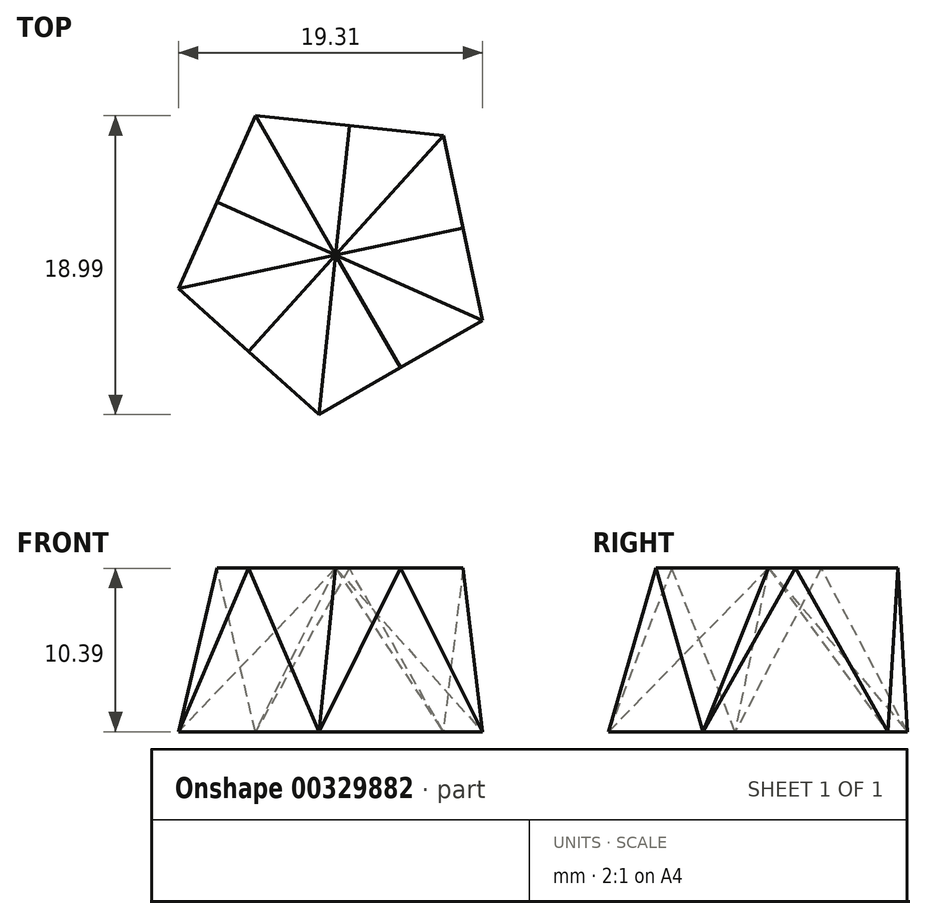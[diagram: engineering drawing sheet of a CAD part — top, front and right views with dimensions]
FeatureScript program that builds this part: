
annotation { "Feature Type Name" : "Feature", "Feature Type Description" : "" }
export const myFeature = defineFeature(function(context is Context, id is Id, definition is map)
    precondition{}
    {
        {
            var Q0;
            Q0=qCreatedBy(makeId("Top.planeOp"),FACE);
            var sketch = newSketch(context, id + "F0", { "sketchPlane" : qUnion([Q0])});
            skLineSegment(sketch, "E0", {"start": v(-6, -8.26) * mm, "end": v(6, -8.26) * mm});
            skLineSegment(sketch, "E1.1.0", {"start": v(6, -8.26) * mm, "end": v(9.7, 3.15) * mm});
            skLineSegment(sketch, "E1.2.0", {"start": v(9.7, 3.15) * mm, "end": v(0, 10.2) * mm});
            skLineSegment(sketch, "E1.3.0", {"start": v(0, 10.2) * mm, "end": v(-9.7, 3.15) * mm});
            skLineSegment(sketch, "E1.4.0", {"start": v(-9.7, 3.15) * mm, "end": v(-6, -8.26) * mm});
            skPoint(sketch, "E1.center", {"position": v(0, 0) * mm});
            skCircle(sketch, "E2", {"center": v(0, 0) * mm, "radius": 8.26 * mm});
            skSolve(sketch);
        }
        {
            var Q0;
            Q0=qCreatedBy(makeId("Front.planeOp"),FACE);
            var sketch = newSketch(context, id + "F1", { "sketchPlane" : qUnion([Q0])});
            skLineSegment(sketch, "E3", {"start": v(-6, 0) * mm, "end": v(0, 10.4) * mm});
            skLineSegment(sketch, "E4", {"start": v(0, 10.4) * mm, "end": v(6, 0) * mm});
            skLineSegment(sketch, "E5", {"start": v(6, 0) * mm, "end": v(-6, 0) * mm});
            skSolve(sketch);
        }
        {
            var Q0;
            Q0 = qSketchRegion(id + "F1", true);
            var Q1;
            Q1=sQuery(id+"F0.wireOp",VERTEX,"E0.start");
            extrude(context, id + "F2", {"entities" : qUnion([Q0]), "endBound" : BoundingType.UP_TO_VERTEX, "depth" : 8.26 * mm, "endBoundEntityVertex" : qUnion([Q1]), "offsetDistance" : 25 * mm});
        }
        {
            var Q0;
            Q0=makeQuery(id+"F2.opExtrude","CAP_FACE",FACE,{"disambiguationData":[OSD([sQuery(id+"F1.wireOp",EDGE,"E3"),sQuery(id+"F1.wireOp",EDGE,"E4"),sQuery(id+"F1.wireOp",EDGE,"E5")])],"isStart":true});
            var sketch = newSketch(context, id + "F3", { "sketchPlane" : qUnion([Q0])});
            skLineSegment(sketch, "E6", {"start": v(0, 0) * mm, "end": v(0, 10.4) * mm});
            skSolve(sketch);
        }
        {
            var Q0;
            Q0=makeQuery(id+"F2.opExtrude","SWEPT_BODY",BODY,{"disambiguationData":[OSD([sQuery(id+"F1.wireOp",EDGE,"E3"),sQuery(id+"F1.wireOp",EDGE,"E4"),sQuery(id+"F1.wireOp",EDGE,"E5")])]});
            var Q1;
            Q1=sQuery(id+"F3.wireOp",EDGE,"E6");
            circularPattern(context, id + "F4", {"operationType" : NewBodyOperationType.ADD, "entities" : qUnion([Q0]), "axis" : qUnion([Q1]), "angle" : 360 * degree, "instanceCount" : 5, "equalSpace" : true});
        }
        {
            var Q0;
            Q0=makeQuery(id+"F2.opExtrude","SWEPT_BODY",BODY,{"disambiguationData":[OSD([sQuery(id+"F1.wireOp",EDGE,"E3"),sQuery(id+"F1.wireOp",EDGE,"E4"),sQuery(id+"F1.wireOp",EDGE,"E5")])]});
            var Q1;
            Q1=sQuery(id+"F0.wireOp",EDGE,"E2");
            transform(context, id + "F5", {"entities" : qUnion([Q0]), "transformType" : TransformType.ROTATION, "transformAxis" : qUnion([Q1]), "angle" : 30 * degree, "makeCopy" : false});
        }
    });
